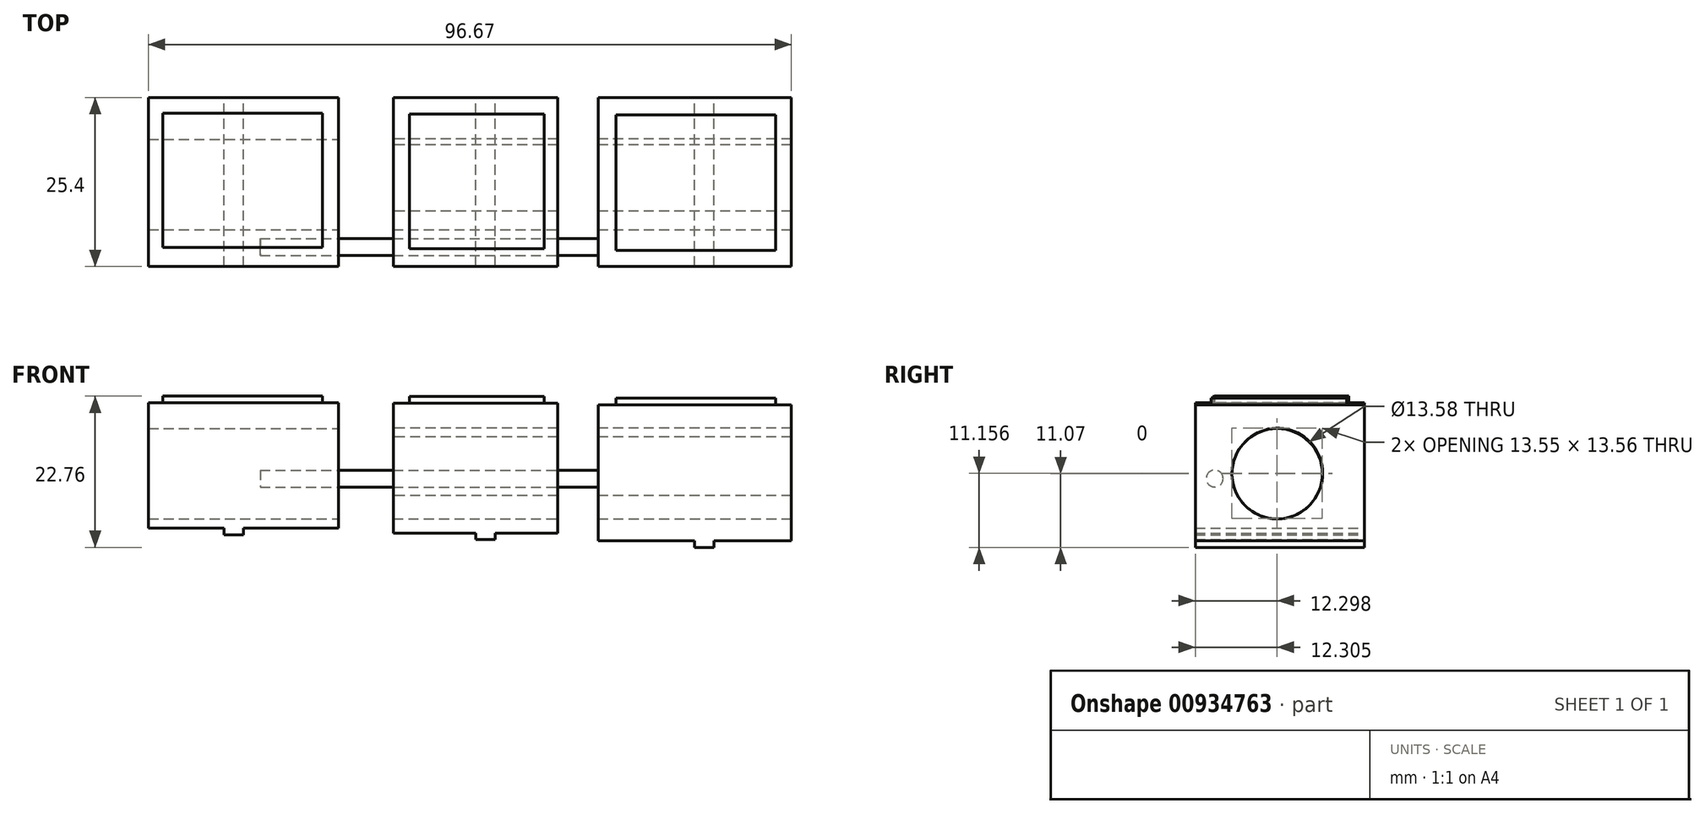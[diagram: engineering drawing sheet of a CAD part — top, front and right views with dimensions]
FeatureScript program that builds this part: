
annotation { "Feature Type Name" : "Feature", "Feature Type Description" : "" }
export const myFeature = defineFeature(function(context is Context, id is Id, definition is map)
    precondition{}
    {
        {
            var Q0;
            Q0=qCreatedBy(makeId("Front.planeOp"),FACE);
            var sketch = newSketch(context, id + "F0", { "sketchPlane" : qUnion([Q0])});
            skLineSegment(sketch, "E0.bottom", {"start": v(42.45, 14.25) * mm, "end": v(71.52, 14.25) * mm});
            skLineSegment(sketch, "E0.top", {"start": v(42.45, 34.68) * mm, "end": v(71.52, 34.68) * mm});
            skLineSegment(sketch, "E0.left", {"start": v(42.45, 14.25) * mm, "end": v(42.45, 34.68) * mm});
            skLineSegment(sketch, "E0.right", {"start": v(71.52, 14.25) * mm, "end": v(71.52, 34.68) * mm});
            skSolve(sketch);
        }
        {
            var Q0;
            Q0 = qSketchRegion(id + "F0", true);
            extrude(context, id + "F1", {"entities" : qUnion([Q0]), "depth" : 25.4 * mm, "offsetDistance" : 25.4 * mm});
        }
        {
            var Q0;
            Q0=qCreatedBy(makeId("Front.planeOp"),FACE);
            var sketch = newSketch(context, id + "F2", { "sketchPlane" : qUnion([Q0])});
            skLineSegment(sketch, "E1.bottom", {"start": v(11.66, 34.97) * mm, "end": v(36.4, 34.97) * mm});
            skLineSegment(sketch, "E1.top", {"start": v(11.66, 15.4) * mm, "end": v(36.4, 15.4) * mm});
            skLineSegment(sketch, "E1.left", {"start": v(11.66, 34.97) * mm, "end": v(11.66, 15.4) * mm});
            skLineSegment(sketch, "E1.right", {"start": v(36.4, 34.97) * mm, "end": v(36.4, 15.4) * mm});
            skPoint(sketch, "E1.middle", {"position": v(24.03, 25.18) * mm});
            skSolve(sketch);
        }
        {
            var Q0;
            Q0 = qSketchRegion(id + "F2", true);
            extrude(context, id + "F3", {"entities" : qUnion([Q0]), "depth" : 25.4 * mm, "offsetDistance" : 25.4 * mm});
        }
        {
            var Q0;
            Q0=qCreatedBy(makeId("Front.planeOp"),FACE);
            var sketch = newSketch(context, id + "F4", { "sketchPlane" : qUnion([Q0])});
            skLineSegment(sketch, "E2.bottom", {"start": v(3.4, 16.13) * mm, "end": v(-25.15, 16.13) * mm});
            skLineSegment(sketch, "E2.top", {"start": v(3.4, 35) * mm, "end": v(-25.15, 35) * mm});
            skLineSegment(sketch, "E2.left", {"start": v(3.4, 16.13) * mm, "end": v(3.4, 35) * mm});
            skLineSegment(sketch, "E2.right", {"start": v(-25.15, 16.13) * mm, "end": v(-25.15, 35) * mm});
            skPoint(sketch, "E2.middle", {"position": v(-10.87, 25.57) * mm});
            skSolve(sketch);
        }
        {
            var Q0;
            Q0 = qSketchRegion(id + "F4", true);
            extrude(context, id + "F5", {"entities" : qUnion([Q0]), "depth" : 25.4 * mm, "offsetDistance" : 25.4 * mm});
        }
        {
            var Q0;
            Q0=makeQuery(id+"F1.opExtrude","SWEPT_FACE",FACE,{"disambiguationData":[OSD([sQuery(id+"F0.wireOp",EDGE,"E0.right")])]});
            var sketch = newSketch(context, id + "F6", { "sketchPlane" : qUnion([Q0])});
            skCircle(sketch, "E3", {"center": v(-13.1, 24.32) * mm, "radius": 6.8 * mm});
            skSolve(sketch);
        }
        {
            var Q0;
            Q0 = qSketchRegion(id + "F6", true);
            extrude(context, id + "F7", {"entities" : qUnion([Q0]), "operationType" : NewBodyOperationType.REMOVE, "oppositeDirection" : true, "depth" : 120 * mm, "offsetDistance" : 25.4 * mm});
        }
        {
            var Q0;
            Q0=makeQuery(id+"FJaOxYqPVvdvAi4_3.boolean.opBoolean","MERGE",FACE,{"derivedFrom":[makeQuery(id+"F5.opExtrude","SWEPT_FACE",FACE,{"disambiguationData":[OSD([sQuery(id+"F4.wireOp",EDGE,"E2.right")])]}),makeQuery(id+"FJaOxYqPVvdvAi4_3.opExtrude","SWEPT_FACE",FACE,{"disambiguationData":[OSD([sQuery(id+"FiqMinOxa8tVhcD_3.wireOp",EDGE,"UDia6Aqh-H9Bv-dTBs-5B6c-KWGi2ay6syEZ.left")])]})]});
            var sketch = newSketch(context, id + "F8", { "sketchPlane" : qUnion([Q0])});
            skCircle(sketch, "E4", {"center": v(13.08, 24.31) * mm, "radius": 6.7 * mm});
            skSolve(sketch);
        }
        {
            var Q0;
            Q0=makeQuery(id+"F8.imprint","IMPRINT",FACE,{"disambiguationData":[TD([[makeQuery(id+"F8.imprint","IMPRINT",EDGE,{"derivedFrom":sQuery(id+"F8.wireOp",EDGE,"E4")}),1.0]])]});
            var Q1;
            Q1=sQuery(id+"F8.wireOp",EDGE,"E4");
            extrude(context, id + "F9", {"entities" : qUnion([Q0]), "operationType" : NewBodyOperationType.REMOVE, "surfaceEntities" : qUnion([Q1]), "oppositeDirection" : true, "depth" : 127 * mm, "offsetDistance" : 25.4 * mm});
        }
        {
            var Q0;
            Q0=makeQuery(id+"F3.opExtrude","SWEPT_FACE",FACE,{"disambiguationData":[OSD([sQuery(id+"F2.wireOp",EDGE,"E1.left")])]});
            var sketch = newSketch(context, id + "F10", { "sketchPlane" : qUnion([Q0])});
            skCircle(sketch, "E5", {"center": v(13, 24.43) * mm, "radius": 6.76 * mm});
            skSolve(sketch);
        }
        {
            var Q0;
            Q0=makeQuery(id+"F10.imprint","IMPRINT",FACE,{"disambiguationData":[TD([[makeQuery(id+"F10.imprint","IMPRINT",EDGE,{"derivedFrom":sQuery(id+"F10.wireOp",EDGE,"E5")}),1.0]])]});
            extrude(context, id + "F11", {"entities" : qUnion([Q0]), "operationType" : NewBodyOperationType.REMOVE, "oppositeDirection" : true, "depth" : 127 * mm, "offsetDistance" : 25.4 * mm});
        }
        {
            var Q0;
            Q0=makeQuery(id+"F1.opExtrude","SWEPT_FACE",FACE,{"disambiguationData":[OSD([sQuery(id+"F0.wireOp",EDGE,"E0.left")])]});
            var sketch = newSketch(context, id + "F12", { "sketchPlane" : qUnion([Q0])});
            skCircle(sketch, "E6", {"center": v(3.38, 24.66) * mm, "radius": 1.27 * mm});
            skSolve(sketch);
        }
        {
            var Q0;
            Q0=sQuery(id+"F12.wireOp",EDGE,"E6");
            extrude(context, id + "F13", {"bodyType" : ToolBodyType.SURFACE, "surfaceEntities" : qUnion([Q0]), "depth" : 40.9 * mm, "offsetDistance" : 25.4 * mm});
        }
        {
            var Q0;
            Q0=makeQuery(id+"F1.opExtrude","SWEPT_FACE",FACE,{"disambiguationData":[OSD([sQuery(id+"F0.wireOp",EDGE,"E0.left")])]});
            var sketch = newSketch(context, id + "F14", { "sketchPlane" : qUnion([Q0])});
            skCircle(sketch, "E7", {"center": v(22.48, 23.6) * mm, "radius": 1.27 * mm});
            skSolve(sketch);
        }
        {
            var Q0;
            Q0 = qSketchRegion(id + "F14", true);
            extrude(context, id + "F15", {"entities" : qUnion([Q0]), "depth" : 50.8 * mm, "offsetDistance" : 25.4 * mm});
        }
        {
            var Q0;
            Q0=makeQuery(id+"F5.opExtrude","SWEPT_FACE",FACE,{"disambiguationData":[OSD([sQuery(id+"F4.wireOp",EDGE,"E2.bottom")])]});
            var sketch = newSketch(context, id + "F16", { "sketchPlane" : qUnion([Q0])});
            skLineSegment(sketch, "E8.bottom", {"start": v(-13.8, 25.4) * mm, "end": v(-10.87, 25.4) * mm});
            skLineSegment(sketch, "E8.top", {"start": v(-13.8, 0) * mm, "end": v(-10.87, 0) * mm});
            skLineSegment(sketch, "E8.left", {"start": v(-13.8, 25.4) * mm, "end": v(-13.8, 0) * mm});
            skLineSegment(sketch, "E8.right", {"start": v(-10.87, 25.4) * mm, "end": v(-10.87, 0) * mm});
            skSolve(sketch);
        }
        {
            var Q0;
            Q0 = qSketchRegion(id + "F16", true);
            extrude(context, id + "F17", {"entities" : qUnion([Q0]), "operationType" : NewBodyOperationType.ADD, "depth" : 1 * mm, "offsetDistance" : 25.4 * mm});
        }
        {
            var Q0;
            Q0=makeQuery(id+"F3.opExtrude","SWEPT_FACE",FACE,{"disambiguationData":[OSD([sQuery(id+"F2.wireOp",EDGE,"E1.top")])]});
            var sketch = newSketch(context, id + "F18", { "sketchPlane" : qUnion([Q0])});
            skLineSegment(sketch, "E9.bottom", {"start": v(24.03, 25.4) * mm, "end": v(27.01, 25.4) * mm});
            skLineSegment(sketch, "E9.top", {"start": v(24.03, 0) * mm, "end": v(27.01, 0) * mm});
            skLineSegment(sketch, "E9.left", {"start": v(24.03, 25.4) * mm, "end": v(24.03, 0) * mm});
            skLineSegment(sketch, "E9.right", {"start": v(27.01, 25.4) * mm, "end": v(27.01, 0) * mm});
            skSolve(sketch);
        }
        {
            var Q0;
            Q0 = qSketchRegion(id + "F18", true);
            extrude(context, id + "F19", {"entities" : qUnion([Q0]), "operationType" : NewBodyOperationType.ADD, "depth" : 1 * mm, "offsetDistance" : 25.4 * mm});
        }
        {
            var Q0;
            Q0=makeQuery(id+"F1.opExtrude","SWEPT_FACE",FACE,{"disambiguationData":[OSD([sQuery(id+"F0.wireOp",EDGE,"E0.bottom")])]});
            var sketch = newSketch(context, id + "F20", { "sketchPlane" : qUnion([Q0])});
            skLineSegment(sketch, "E10.bottom", {"start": v(56.99, 25.4) * mm, "end": v(59.9, 25.4) * mm});
            skLineSegment(sketch, "E10.top", {"start": v(56.99, 0) * mm, "end": v(59.9, 0) * mm});
            skLineSegment(sketch, "E10.left", {"start": v(56.99, 25.4) * mm, "end": v(56.99, 0) * mm});
            skLineSegment(sketch, "E10.right", {"start": v(59.9, 25.4) * mm, "end": v(59.9, 0) * mm});
            skSolve(sketch);
        }
        {
            var Q0;
            Q0 = qSketchRegion(id + "F20", true);
            extrude(context, id + "F21", {"entities" : qUnion([Q0]), "operationType" : NewBodyOperationType.ADD, "depth" : 1 * mm, "offsetDistance" : 25.4 * mm});
        }
        {
            var Q0;
            Q0=makeQuery(id+"F5.opExtrude","SWEPT_FACE",FACE,{"disambiguationData":[OSD([sQuery(id+"F4.wireOp",EDGE,"E2.top")])]});
            var sketch = newSketch(context, id + "F22", { "sketchPlane" : qUnion([Q0])});
            skLineSegment(sketch, "E11.bottom", {"start": v(-23, -2.35) * mm, "end": v(1.03, -2.35) * mm});
            skLineSegment(sketch, "E11.top", {"start": v(-23, -22.52) * mm, "end": v(1.03, -22.52) * mm});
            skLineSegment(sketch, "E11.left", {"start": v(-23, -2.35) * mm, "end": v(-23, -22.52) * mm});
            skLineSegment(sketch, "E11.right", {"start": v(1.03, -2.35) * mm, "end": v(1.03, -22.52) * mm});
            skSolve(sketch);
        }
        {
            var Q0;
            Q0=makeQuery(id+"F22.imprint","IMPRINT",FACE,{"disambiguationData":[TD([[makeQuery(id+"F22.imprint","IMPRINT",EDGE,{"derivedFrom":sQuery(id+"F22.wireOp",EDGE,"E11.bottom")}),-1.0]])]});
            extrude(context, id + "F23", {"entities" : qUnion([Q0]), "operationType" : NewBodyOperationType.ADD, "depth" : 1 * mm, "offsetDistance" : 25.4 * mm});
        }
        {
            var Q0;
            Q0=makeQuery(id+"F3.opExtrude","SWEPT_FACE",FACE,{"disambiguationData":[OSD([sQuery(id+"F2.wireOp",EDGE,"E1.bottom")])]});
            var sketch = newSketch(context, id + "F24", { "sketchPlane" : qUnion([Q0])});
            skLineSegment(sketch, "E12.bottom", {"start": v(14.07, -2.47) * mm, "end": v(34.37, -2.47) * mm});
            skLineSegment(sketch, "E12.top", {"start": v(14.07, -22.75) * mm, "end": v(34.37, -22.75) * mm});
            skLineSegment(sketch, "E12.left", {"start": v(14.07, -2.47) * mm, "end": v(14.07, -22.75) * mm});
            skLineSegment(sketch, "E12.right", {"start": v(34.37, -2.47) * mm, "end": v(34.37, -22.75) * mm});
            skSolve(sketch);
        }
        {
            var Q0;
            Q0=makeQuery(id+"F24.imprint","IMPRINT",FACE,{"disambiguationData":[TD([[makeQuery(id+"F24.imprint","IMPRINT",EDGE,{"derivedFrom":sQuery(id+"F24.wireOp",EDGE,"E12.bottom")}),-1.0]])]});
            extrude(context, id + "F25", {"entities" : qUnion([Q0]), "operationType" : NewBodyOperationType.ADD, "depth" : 1 * mm, "offsetDistance" : 25.4 * mm});
        }
        {
            var Q0;
            Q0=makeQuery(id+"F1.opExtrude","SWEPT_FACE",FACE,{"disambiguationData":[OSD([sQuery(id+"F0.wireOp",EDGE,"E0.top")])]});
            var sketch = newSketch(context, id + "F26", { "sketchPlane" : qUnion([Q0])});
            skLineSegment(sketch, "E13.bottom", {"start": v(45.14, -2.61) * mm, "end": v(69.15, -2.61) * mm});
            skLineSegment(sketch, "E13.top", {"start": v(45.14, -23) * mm, "end": v(69.15, -23) * mm});
            skLineSegment(sketch, "E13.left", {"start": v(45.14, -2.61) * mm, "end": v(45.14, -23) * mm});
            skLineSegment(sketch, "E13.right", {"start": v(69.15, -2.61) * mm, "end": v(69.15, -23) * mm});
            skSolve(sketch);
        }
        {
            var Q0;
            Q0=makeQuery(id+"F26.imprint","IMPRINT",FACE,{"disambiguationData":[TD([[makeQuery(id+"F26.imprint","IMPRINT",EDGE,{"derivedFrom":sQuery(id+"F26.wireOp",EDGE,"E13.bottom")}),-1.0]])]});
            extrude(context, id + "F27", {"entities" : qUnion([Q0]), "operationType" : NewBodyOperationType.ADD, "depth" : 1 * mm, "offsetDistance" : 25.4 * mm});
        }
    });
